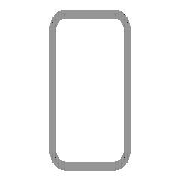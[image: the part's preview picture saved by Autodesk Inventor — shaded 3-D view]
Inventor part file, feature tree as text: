
AUTODESK INVENTOR PART (.ipt)
format: ipt  version: 2025 (Build 290162010, 162A)  size: 131,584 bytes
history: native  units: mm (DEFAULTED — no unit token found)
features: other x4, sketch x1, plane x1
ambient origin geometry x8: Origin, YZ Plane, XZ Plane, XY Plane, X Axis, Y Axis, Z Axis, Center Point
bodies: Solid1 (feature_tree), Body (feature_tree)
feature tree (6):
  parser-record x1  (decoder bookkeeping rows leaked as tree rows — omitted from the tree; the rows remain in map.json)
  other  "Driven Length"
  other  "Start Plane"
  other  "End Plane"
  sketch  "Sketch3"  dims[d3=1050.0mm d4=0.0mm d7=6.0mm d9=40.0mm d11=80.0mm d12=3.0mm d13=-0.0mm d14=1050.0mm d15=20.0mm d16=40.0mm d17=90.0deg d18=1050.0mm]
  plane  "Work Plane3"
